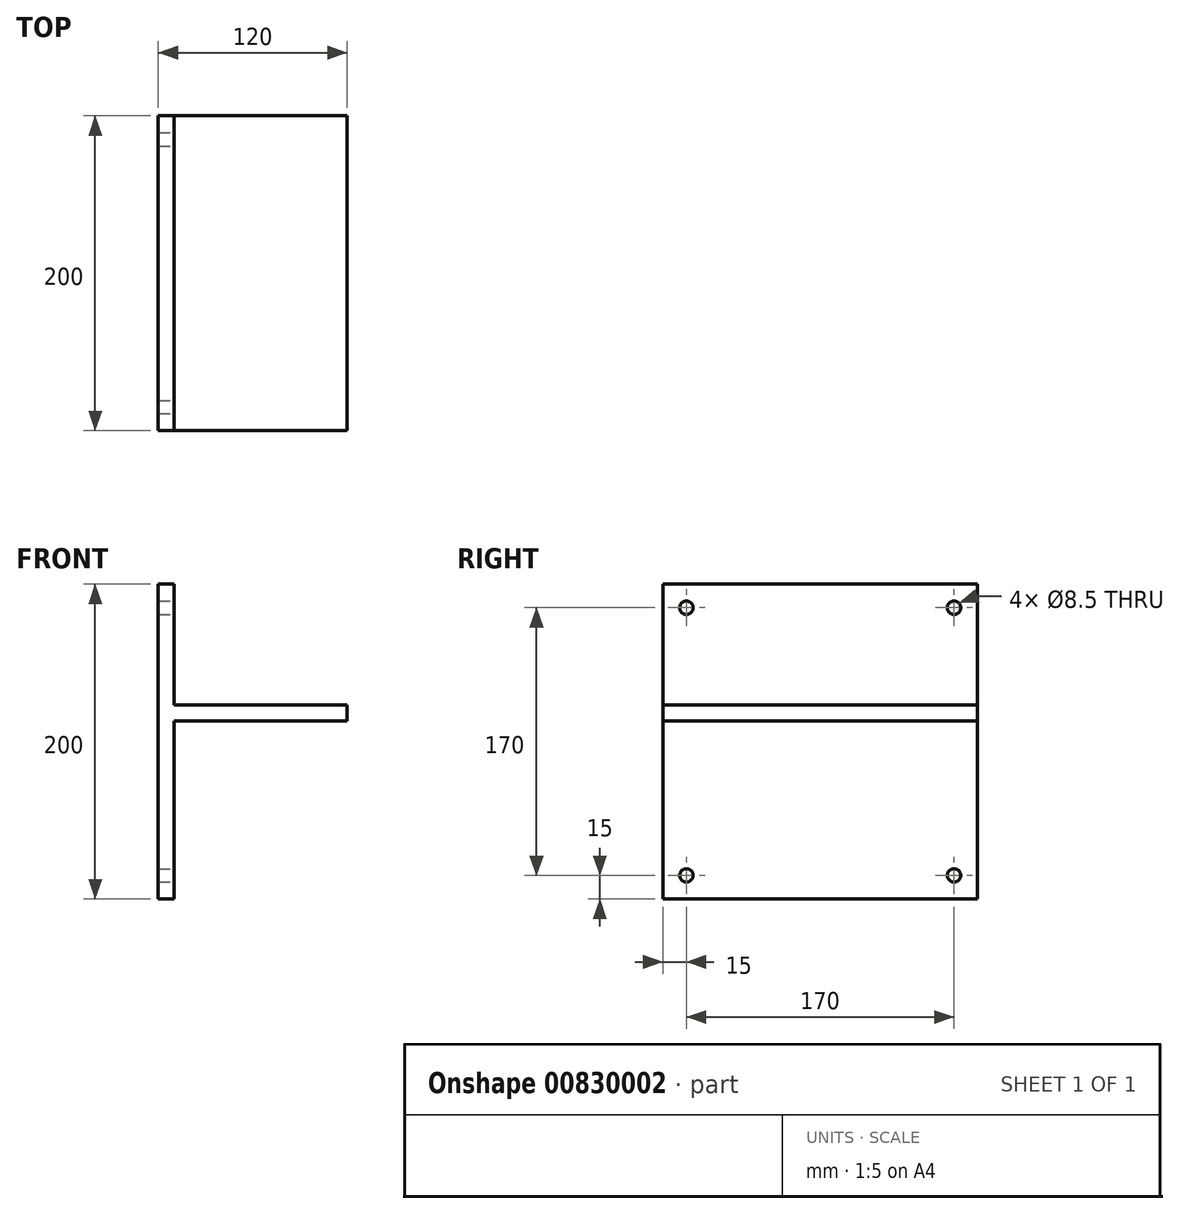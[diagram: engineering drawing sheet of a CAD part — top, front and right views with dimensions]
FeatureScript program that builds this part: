
annotation { "Feature Type Name" : "Feature", "Feature Type Description" : "" }
export const myFeature = defineFeature(function(context is Context, id is Id, definition is map)
    precondition{}
    {
        {
            var Q0;
            Q0=qCreatedBy(makeId("Front.planeOp"),FACE);
            var sketch = newSketch(context, id + "F0", { "sketchPlane" : qUnion([Q0])});
            skLineSegment(sketch, "E0", {"start": v(-17.42, 92.2) * mm, "end": v(-17.42, -107.8) * mm});
            skLineSegment(sketch, "E1", {"start": v(-7.42, 5.4) * mm, "end": v(-7.42, -107.8) * mm});
            skLineSegment(sketch, "E2", {"start": v(-7.42, 5.4) * mm, "end": v(102.58, 5.4) * mm});
            skLineSegment(sketch, "E3", {"start": v(-7.42, 15.4) * mm, "end": v(102.58, 15.4) * mm});
            skLineSegment(sketch, "E4", {"start": v(-17.42, -107.8) * mm, "end": v(-7.42, -107.8) * mm});
            skLineSegment(sketch, "E5", {"start": v(-7.42, 15.4) * mm, "end": v(-7.42, 92.2) * mm});
            skLineSegment(sketch, "E6", {"start": v(-17.42, 92.2) * mm, "end": v(-7.42, 92.2) * mm});
            skLineSegment(sketch, "E7", {"start": v(102.58, 15.4) * mm, "end": v(102.58, 5.4) * mm});
            skLineSegment(sketch, "E8", {"start": v(-7.42, 5.4) * mm, "end": v(62.58, 5.4) * mm});
            skLineSegment(sketch, "E9", {"start": v(-7.42, 5.4) * mm, "end": v(-7.42, -64.6) * mm});
            skLineSegment(sketch, "E10", {"start": v(-7.42, -64.6) * mm, "end": v(62.58, 5.4) * mm});
            skSolve(sketch);
        }
        {
            var Q0;
            Q0=makeQuery(id+"F0.imprint","IMPRINT",FACE,{"disambiguationData":[TD([[makeQuery(id+"F0.imprint","IMPRINT",EDGE,{"derivedFrom":sQuery(id+"F0.wireOp",EDGE,"E0")}),1.0]])]});
            extrude(context, id + "F1", {"entities" : qUnion([Q0]), "depth" : 200 * mm, "offsetDistance" : 25 * mm});
        }
        {
            var Q0;
            Q0=makeQuery(id+"F1.opExtrude","SWEPT_FACE",FACE,{"disambiguationData":[OSD([sQuery(id+"F0.wireOp",EDGE,"E5")])]});
            var sketch = newSketch(context, id + "F2", { "sketchPlane" : qUnion([Q0])});
            skCircle(sketch, "E11", {"center": v(-185, 77.2) * mm, "radius": 4.25 * mm});
            skCircle(sketch, "E12", {"center": v(-185, -92.8) * mm, "radius": 4.25 * mm});
            skCircle(sketch, "E13", {"center": v(-15, 77.2) * mm, "radius": 4.25 * mm});
            skCircle(sketch, "E14", {"center": v(-15, -92.8) * mm, "radius": 4.25 * mm});
            skSolve(sketch);
        }
        {
            var Q0;
            Q0=makeQuery(id+"F2.imprint","IMPRINT",FACE,{"disambiguationData":[TD([[makeQuery(id+"F2.imprint","IMPRINT",EDGE,{"derivedFrom":sQuery(id+"F2.wireOp",EDGE,"E11")}),1.0]])]});
            var Q1;
            Q1=makeQuery(id+"F2.imprint","IMPRINT",FACE,{"disambiguationData":[TD([[makeQuery(id+"F2.imprint","IMPRINT",EDGE,{"derivedFrom":sQuery(id+"F2.wireOp",EDGE,"E13")}),1.0]])]});
            var Q2;
            Q2=makeQuery(id+"F2.imprint","IMPRINT",FACE,{"disambiguationData":[TD([[makeQuery(id+"F2.imprint","IMPRINT",EDGE,{"derivedFrom":sQuery(id+"F2.wireOp",EDGE,"E12")}),1.0]])]});
            var Q3;
            Q3=makeQuery(id+"F2.imprint","IMPRINT",FACE,{"disambiguationData":[TD([[makeQuery(id+"F2.imprint","IMPRINT",EDGE,{"derivedFrom":sQuery(id+"F2.wireOp",EDGE,"E14")}),1.0]])]});
            extrude(context, id + "F3", {"entities" : qUnion([Q0, Q1, Q2, Q3]), "operationType" : NewBodyOperationType.REMOVE, "oppositeDirection" : true, "depth" : 25 * mm, "offsetDistance" : 25 * mm});
        }
    });
